# Revit family: Lav.Public Temporizado
name_source: partatom
category: Plumbing Fixtures
revit_build: Autodesk Revit 2015 (Build: 20140322_1515(x64)
units: mm (PartAtom-declared; Revit-internal decimal feet)

## types (1)
- Lav. Public Temporizado
    Assembly Code = D2010.60
    BT_Color = Cromo
    BT_Itemizado_Estandar_CDT = E 04 02 00
    BT_Material = Latón Cromado
    BT_SKU = 00 00 00
    BT_Uso = Grifería
    Default Elevation = 1219 mm
    Depth = 105 mm
    Description = Grifo temporizado
    Height = 90 mm
    ID_Objeto = BT_F_F_1814
    ID_Source = BIMTOOL
    Keynote = 22 31 13
    Manufacturer = Klipen
    Model = Lav. Public Temporizado
    Supplier = Mk
    Type Comments = Grifo temporizado Public
Presión de trabajo: 2 a 4 BAR
Tiempo regulado: 6 segundos aprox.
Caudal: 12 lts /min
1,2 lpc 
Terminación: Cromo
    URL = www.bimtool.com
    Width = 29 mm

## geometry (parser evidence)
native form markers: Blend x6, Extrusion x2, Sweep x5
no freeform markers — native parametric forms only
